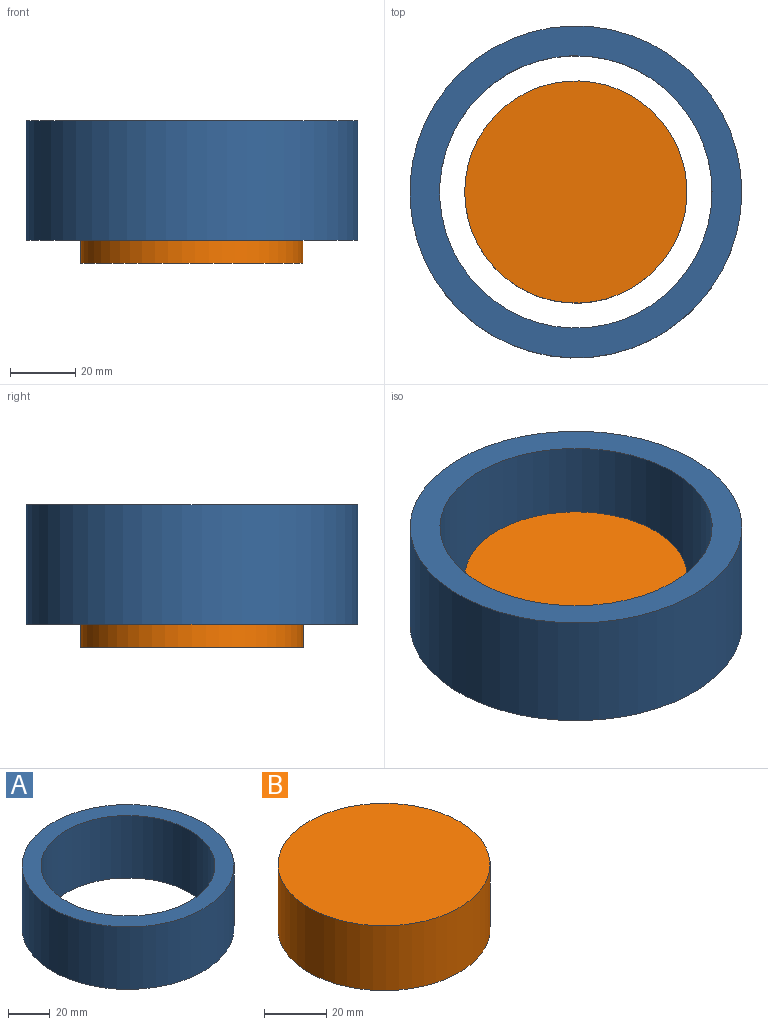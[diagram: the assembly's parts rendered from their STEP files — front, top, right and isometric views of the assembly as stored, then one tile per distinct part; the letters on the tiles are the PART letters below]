
ASSEMBLY  parts=2 mates=2
PART A: 4 faces, bbox 101.4x101.4x36.6 mm
  f0: cylinder r=41.61mm len=83.21mm, axis (0,0,-1), area 9561.5mm2, adj f2,f3
  f1: cylinder r=50.71mm len=101.42mm, axis (0,0,-1), area 11653.5mm2, adj f2,f3
  f2: plane 101.42x101.42mm, normal (0,0,1), area 2640mm2, adj f0,f1
  f3: plane 101.42x101.42mm, normal (0,0,-1), area 2640mm2, adj f0,f1
PART B: 3 faces, bbox 67.9x67.9x25.4 mm
  f0: cylinder r=33.95mm len=67.9mm, axis (0,0,-1), area 5417.8mm2, adj f1,f2
  f1: plane 67.9x67.9mm, normal (0,0,1), area 3620.5mm2, adj f0
  f2: plane 67.9x67.9mm, normal (0,0,-1), area 3620.5mm2, adj f0
PLACE A t=(-33.34,3.65,16.06)mm
PLACE B rot(axis=(0,0,1),180deg) t=(-33.34,3.65,-70.55)mm
MATE slider B.f0 <-> A.f1  axis (0,0,1) through (-33.34,3.65,34.35)mm
MATE parallel B.f0 <-> A.f1  axis (0,0,1) through (-33.34,3.65,34.35)mm
